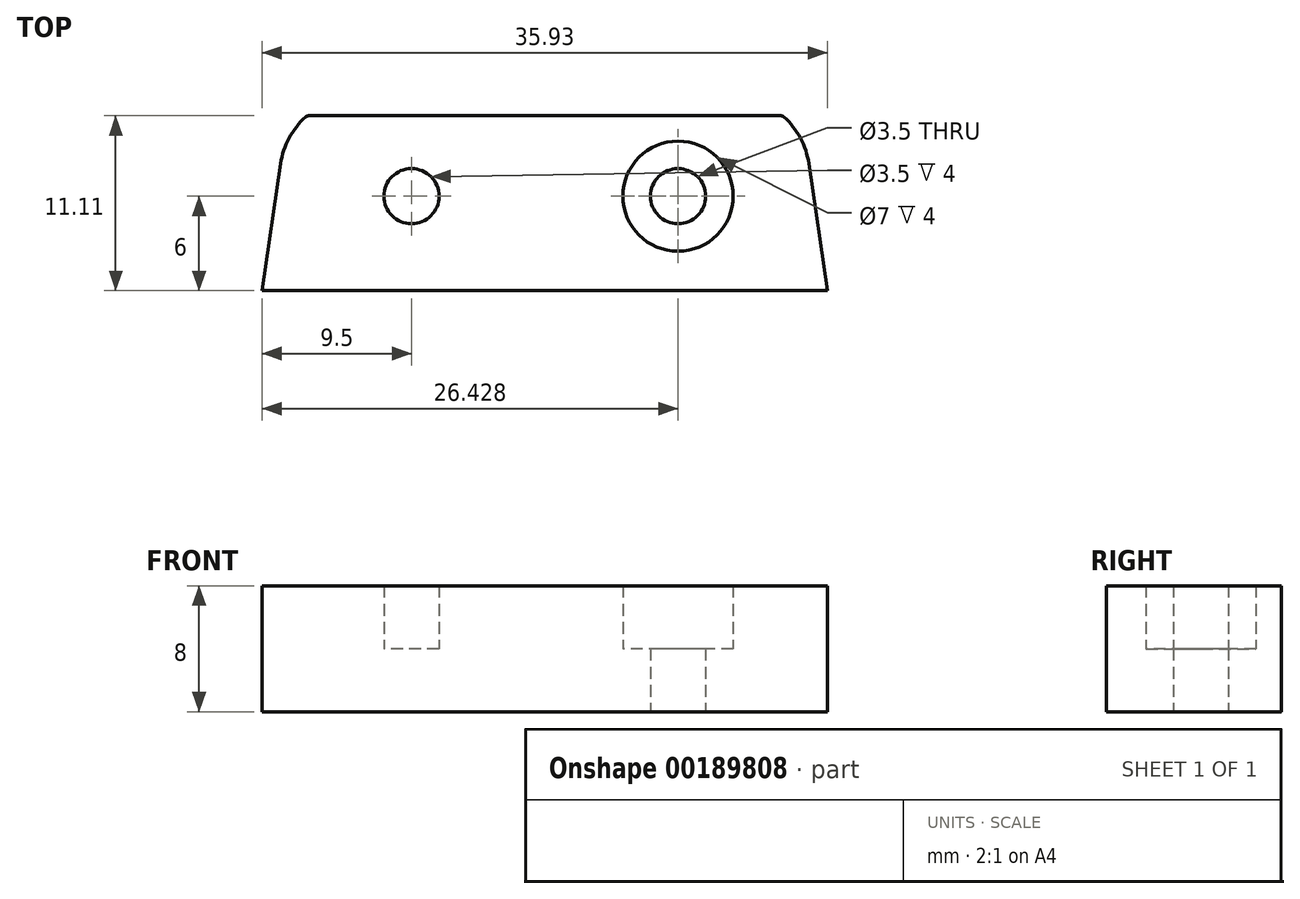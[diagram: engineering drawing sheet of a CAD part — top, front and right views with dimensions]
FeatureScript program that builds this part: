
annotation { "Feature Type Name" : "Feature", "Feature Type Description" : "" }
export const myFeature = defineFeature(function(context is Context, id is Id, definition is map)
    precondition{}
    {
        {
            var Q0;
            Q0=qCreatedBy(makeId("Top.planeOp"),FACE);
            var sketch = newSketch(context, id + "F0", { "sketchPlane" : qUnion([Q0])});
            skLineSegment(sketch, "E0", {"start": v(-19, 0) * mm, "end": v(-17.8, 8.07) * mm});
            skLineSegment(sketch, "E1", {"start": v(-11.13, 15.48) * mm, "end": v(-16.15, 11.1) * mm});
            skCircle(sketch, "E2", {"center": v(-9.5, 6) * mm, "radius": 3.5 * mm});
            skCircle(sketch, "E3", {"center": v(-9.5, 6) * mm, "radius": 1.75 * mm});
            skArc(sketch, "E4", {"start": v(-1.04, 28.23) * mm, "mid": v(-5.58, 26.7) * mm, "end": v(-8.26, 22.73) * mm});
            skLineSegment(sketch, "E5", {"start": v(-9.6, 17.91) * mm, "end": v(-8.26, 22.73) * mm});
            skPoint(sketch, "E6.visualSharp", {"position": v(-10, 16.46) * mm});
            skArc(sketch, "E6.filletArc", {"start": v(-11.13, 15.48) * mm, "mid": v(-10.19, 16.58) * mm, "end": v(-9.6, 17.91) * mm});
            skPoint(sketch, "E7.visualSharp", {"position": v(7.93, 16.46) * mm});
            skArc(sketch, "E8", {"start": v(-1.04, 24.35) * mm, "mid": v(-4.66, 20.73) * mm, "end": v(-1.04, 17.1) * mm});
            skPoint(sketch, "E9.visualSharp", {"position": v(-17.54, 9.9) * mm});
            skArc(sketch, "E9.filletArc", {"start": v(-16.23, 11.03) * mm, "mid": v(-17.27, 9.69) * mm, "end": v(-17.8, 8.07) * mm});
            skPoint(sketch, "E10.visualSharp", {"position": v(15.47, 9.9) * mm});
            skArc(sketch, "E11.MirrorCS", {"start": v(-1.04, 28.23) * mm, "mid": v(3.5, 26.7) * mm, "end": v(6.2, 22.73) * mm});
            skLineSegment(sketch, "E12.MirrorCS", {"start": v(7.53, 17.91) * mm, "end": v(6.2, 22.73) * mm});
            skArc(sketch, "E13.MirrorCS", {"start": v(9.06, 15.48) * mm, "mid": v(8.11, 16.58) * mm, "end": v(7.53, 17.91) * mm});
            skLineSegment(sketch, "E14.MirrorCS", {"start": v(9.06, 15.48) * mm, "end": v(14.08, 11.1) * mm});
            skArc(sketch, "E15.MirrorCS", {"start": v(14.16, 11.03) * mm, "mid": v(15.2, 9.69) * mm, "end": v(15.74, 8.07) * mm});
            skLineSegment(sketch, "E16.MirrorCS", {"start": v(16.93, 0) * mm, "end": v(15.74, 8.07) * mm});
            skArc(sketch, "E17.MirrorCS", {"start": v(-1.04, 24.35) * mm, "mid": v(2.59, 20.73) * mm, "end": v(-1.04, 17.1) * mm});
            skCircle(sketch, "E18.MirrorC", {"center": v(7.43, 6) * mm, "radius": 3.5 * mm});
            skCircle(sketch, "E19.MirrorC", {"center": v(7.43, 6) * mm, "radius": 1.75 * mm});
            skLineSegment(sketch, "E20", {"start": v(-19, 0) * mm, "end": v(16.93, 0) * mm});
            skLineSegment(sketch, "E21", {"start": v(-16.04, 11.1) * mm, "end": v(13.97, 11.1) * mm});
            skPoint(sketch, "E22.visualSharp", {"position": v(-16.15, 11.1) * mm});
            skArc(sketch, "E22.filletArc", {"start": v(-16.04, 11.1) * mm, "mid": v(-16.14, 11.09) * mm, "end": v(-16.23, 11.03) * mm});
            skPoint(sketch, "E23.visualSharp", {"position": v(14.08, 11.1) * mm});
            skArc(sketch, "E23.filletArc", {"start": v(14.16, 11.03) * mm, "mid": v(14.07, 11.09) * mm, "end": v(13.97, 11.1) * mm});
            skSolve(sketch);
        }
        {
            var Q0;
            Q0=makeQuery(id+"F0.imprint","IMPRINT",FACE,{"disambiguationData":[TD([[makeQuery(id+"F0.imprint","IMPRINT",EDGE,{"derivedFrom":sQuery(id+"F0.wireOp",EDGE,"Ru46J3V1-BN9A-t4EI-RGMb-jq8WFDNxCXXq")}),-1.0]])]});
            var Q1;
            Q1=makeQuery(id+"F0.imprint","IMPRINT",FACE,{"disambiguationData":[TD([[makeQuery(id+"F0.imprint","IMPRINT",EDGE,{"derivedFrom":sQuery(id+"F0.wireOp",EDGE,"vD3NZcdB-SgQG-xxm7-EOxV-P0EttlGTzlga")}),-1.0]])]});
            var Q2;
            Q2=makeQuery(id+"F0.imprint","IMPRINT",FACE,{"disambiguationData":[TD([[makeQuery(id+"F0.imprint","IMPRINT",EDGE,{"derivedFrom":sQuery(id+"F0.wireOp",EDGE,"E0")}),-1.0]])]});
            extrude(context, id + "F1", {"entities" : qUnion([Q0, Q1, Q2]), "depth" : 4 * mm});
        }
        {
            var Q0;
            Q0=makeQuery(id+"F0.imprint","IMPRINT",FACE,{"disambiguationData":[TD([[makeQuery(id+"F0.imprint","IMPRINT",EDGE,{"derivedFrom":sQuery(id+"F0.wireOp",EDGE,"3bpybDuj-MZcf-nzSA-y5HP-1Ucw2PFUD1lN")}),1.0]])]});
            var Q1;
            Q1=makeQuery(id+"F0.imprint","IMPRINT",FACE,{"disambiguationData":[TD([[makeQuery(id+"F0.imprint","IMPRINT",EDGE,{"derivedFrom":sQuery(id+"F0.wireOp",EDGE,"7a818348-4feb-4938-b127-ce05c0f473900.MirrorC")}),-1.0]])]});
            var Q2;
            Q2=makeQuery(id+"F0.imprint","IMPRINT",FACE,{"disambiguationData":[TD([[makeQuery(id+"F0.imprint","IMPRINT",EDGE,{"derivedFrom":sQuery(id+"F0.wireOp",EDGE,"c41f1a25-7c1b-449b-8bbe-a3a773eef9f20.MirrorC")}),1.0]])]});
            var Q3;
            Q3=makeQuery(id+"F0.imprint","IMPRINT",FACE,{"disambiguationData":[TD([[makeQuery(id+"F0.imprint","IMPRINT",EDGE,{"derivedFrom":sQuery(id+"F0.wireOp",EDGE,"YZ3jdz4Q-1nQX-V1tv-PDWv-eDCCawTp6CNW")}),1.0]])]});
            var Q4;
            Q4=makeQuery(id+"F0.imprint","IMPRINT",FACE,{"disambiguationData":[TD([[makeQuery(id+"F0.imprint","IMPRINT",EDGE,{"derivedFrom":sQuery(id+"F0.wireOp",EDGE,"dc8b8af6-f884-4445-9d73-5954fea702aa0.MirrorC")}),1.0]])]});
            var Q5;
            Q5=makeQuery(id+"F0.imprint","IMPRINT",FACE,{"disambiguationData":[TD([[makeQuery(id+"F0.imprint","IMPRINT",EDGE,{"derivedFrom":sQuery(id+"F0.wireOp",EDGE,"E3")}),1.0]])]});
            var Q6;
            Q6=makeQuery(id+"F0.imprint","IMPRINT",FACE,{"disambiguationData":[TD([[makeQuery(id+"F0.imprint","IMPRINT",EDGE,{"derivedFrom":sQuery(id+"F0.wireOp",EDGE,"E19.MirrorC")}),-1.0]])]});
            extrude(context, id + "F2", {"entities" : qUnion([Q0, Q1, Q2, Q3, Q4, Q5, Q6]), "operationType" : NewBodyOperationType.ADD, "depth" : 4 * mm});
        }
        {
            var Q0;
            Q0=makeQuery(id+"F0.imprint","IMPRINT",FACE,{"disambiguationData":[TD([[makeQuery(id+"F0.imprint","IMPRINT",EDGE,{"derivedFrom":sQuery(id+"F0.wireOp",EDGE,"MXIdjOEz-8Rl6-3WYY-fViL-0X2qQpVSmeco")}),1.0]])]});
            var Q1;
            Q1=makeQuery(id+"F0.imprint","IMPRINT",FACE,{"disambiguationData":[TD([[makeQuery(id+"F0.imprint","IMPRINT",EDGE,{"derivedFrom":sQuery(id+"F0.wireOp",EDGE,"0cc1a50b-0361-4aee-806f-dfb6b972d0bb0.MirrorC")}),-1.0]])]});
            var Q2;
            Q2=makeQuery(id+"F0.imprint","IMPRINT",FACE,{"disambiguationData":[TD([[makeQuery(id+"F0.imprint","IMPRINT",EDGE,{"derivedFrom":sQuery(id+"F0.wireOp",EDGE,"c41f1a25-7c1b-449b-8bbe-a3a773eef9f20.MirrorC")}),-1.0]])]});
            var Q3;
            Q3=makeQuery(id+"F0.imprint","IMPRINT",FACE,{"disambiguationData":[TD([[makeQuery(id+"F0.imprint","IMPRINT",EDGE,{"derivedFrom":sQuery(id+"F0.wireOp",EDGE,"pKkQPfjk-ymGL-uVOI-PXtK-5nXTyFiCnjMW")}),1.0]])]});
            var Q4;
            Q4=makeQuery(id+"F0.imprint","IMPRINT",FACE,{"disambiguationData":[TD([[makeQuery(id+"F0.imprint","IMPRINT",EDGE,{"derivedFrom":sQuery(id+"F0.wireOp",EDGE,"dc8b8af6-f884-4445-9d73-5954fea702aa0.MirrorC")}),-1.0]])]});
            var Q5;
            Q5=makeQuery(id+"F0.imprint","IMPRINT",FACE,{"disambiguationData":[TD([[makeQuery(id+"F0.imprint","IMPRINT",EDGE,{"derivedFrom":sQuery(id+"F0.wireOp",EDGE,"E2")}),1.0]])]});
            var Q6;
            Q6=makeQuery(id+"F0.imprint","IMPRINT",FACE,{"disambiguationData":[TD([[makeQuery(id+"F0.imprint","IMPRINT",EDGE,{"derivedFrom":sQuery(id+"F0.wireOp",EDGE,"E18.MirrorC")}),-1.0]])]});
            extrude(context, id + "F3", {"entities" : qUnion([Q0, Q1, Q2, Q3, Q4, Q5, Q6]), "operationType" : NewBodyOperationType.ADD, "depth" : 8 * mm});
        }
    });
